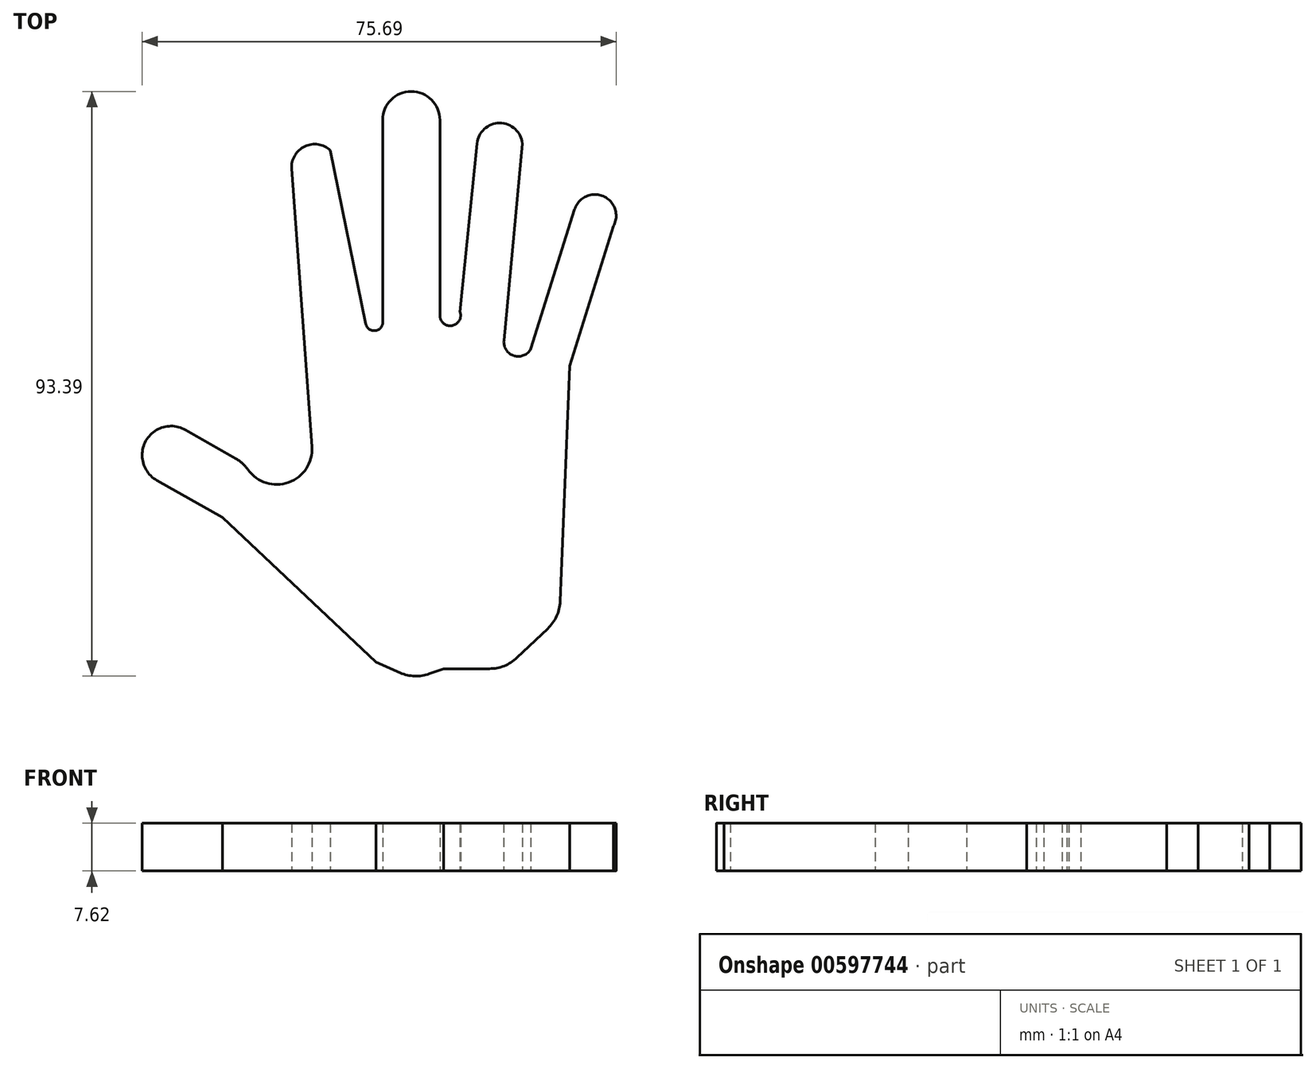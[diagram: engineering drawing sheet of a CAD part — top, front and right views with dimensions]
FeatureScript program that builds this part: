
annotation { "Feature Type Name" : "Feature", "Feature Type Description" : "" }
export const myFeature = defineFeature(function(context is Context, id is Id, definition is map)
    precondition{}
    {
        {
            var Q0;
            Q0=qCreatedBy(makeId("Top.planeOp"),FACE);
            var sketch = newSketch(context, id + "F0", { "sketchPlane" : qUnion([Q0])});
            skLineSegment(sketch, "E0", {"start": v(-29.58, 47.06) * mm, "end": v(-26.36, 2.69) * mm});
            skLineSegment(sketch, "E1", {"start": v(-23.4, 50.02) * mm, "end": v(-17.75, 22.32) * mm});
            skLineSegment(sketch, "E2", {"start": v(-15.06, 54.86) * mm, "end": v(-15.06, 22.32) * mm});
            skLineSegment(sketch, "E3", {"start": v(-5.92, 54.86) * mm, "end": v(-5.92, 23.67) * mm});
            skLineSegment(sketch, "E4", {"start": v(0, 51.1) * mm, "end": v(-2.69, 24.2) * mm});
            skLineSegment(sketch, "E5", {"start": v(7.26, 51.1) * mm, "end": v(4.3, 19.63) * mm});
            skLineSegment(sketch, "E6", {"start": v(15.6, 40.61) * mm, "end": v(8.61, 18.31) * mm});
            skLineSegment(sketch, "E7", {"start": v(21.78, 37.92) * mm, "end": v(14.8, 15.6) * mm});
            skLineSegment(sketch, "E8", {"start": v(14.8, 15.6) * mm, "end": v(13.27, -22) * mm});
            skLineSegment(sketch, "E9", {"start": v(-40.61, -8.6) * mm, "end": v(-16.14, -31.74) * mm});
            skLineSegment(sketch, "E10", {"start": v(-40.61, -8.6) * mm, "end": v(-51.1, -2.69) * mm});
            skLineSegment(sketch, "E11", {"start": v(11.3, -26.36) * mm, "end": v(6.37, -31.02) * mm});
            skLineSegment(sketch, "E12", {"start": v(2, -32.76) * mm, "end": v(-5.34, -32.76) * mm});
            skLineSegment(sketch, "E13", {"start": v(-5.34, -32.76) * mm, "end": v(-7.58, -33.57) * mm});
            skLineSegment(sketch, "E14", {"start": v(-12.26, -33.42) * mm, "end": v(-16.14, -31.74) * mm});
            skPoint(sketch, "E15.visualSharp", {"position": v(-9.95, -34.42) * mm});
            skArc(sketch, "E15.filletArc", {"start": v(-12.26, -33.42) * mm, "mid": v(-9.94, -33.94) * mm, "end": v(-7.58, -33.57) * mm});
            skPoint(sketch, "E16.visualSharp", {"position": v(4.53, -32.76) * mm});
            skArc(sketch, "E16.filletArc", {"start": v(2, -32.76) * mm, "mid": v(4.35, -32.31) * mm, "end": v(6.37, -31.02) * mm});
            skPoint(sketch, "E17.visualSharp", {"position": v(13.17, -24.58) * mm});
            skArc(sketch, "E17.filletArc", {"start": v(11.3, -26.36) * mm, "mid": v(12.7, -24.37) * mm, "end": v(13.27, -22) * mm});
            skArc(sketch, "E18", {"start": v(-17.75, 22.32) * mm, "mid": v(-16.4, 21.22) * mm, "end": v(-15.06, 22.32) * mm});
            skArc(sketch, "E19", {"start": v(-5.92, 23.67) * mm, "mid": v(-3.99, 22.03) * mm, "end": v(-2.69, 24.2) * mm});
            skArc(sketch, "E20", {"start": v(4.3, 19.63) * mm, "mid": v(5.92, 17.22) * mm, "end": v(8.61, 18.31) * mm});
            skArc(sketch, "E21", {"start": v(-26.36, 2.69) * mm, "mid": v(-30.06, -3.01) * mm, "end": v(-36.55, -1) * mm});
            skArc(sketch, "E22", {"start": v(-51.1, -2.69) * mm, "mid": v(-52.85, 3.64) * mm, "end": v(-46.53, 5.38) * mm});
            skLineSegment(sketch, "E23", {"start": v(-46.53, 5.38) * mm, "end": v(-38.56, 0.83) * mm});
            skPoint(sketch, "E24.visualSharp", {"position": v(-37.11, 0) * mm});
            skArc(sketch, "E24.filletArc", {"start": v(-36.55, -1) * mm, "mid": v(-37.46, 0.03) * mm, "end": v(-38.56, 0.83) * mm});
            skArc(sketch, "E25", {"start": v(-29.58, 47.06) * mm, "mid": v(-27.5, 50.65) * mm, "end": v(-23.4, 50.02) * mm});
            skArc(sketch, "E26", {"start": v(-15.06, 54.86) * mm, "mid": v(-10.49, 59.44) * mm, "end": v(-5.92, 54.86) * mm});
            skArc(sketch, "E27", {"start": v(0, 51.1) * mm, "mid": v(3.63, 54.38) * mm, "end": v(7.26, 51.1) * mm});
            skArc(sketch, "E28", {"start": v(15.6, 40.61) * mm, "mid": v(20.19, 42.7) * mm, "end": v(21.78, 37.92) * mm});
            skSolve(sketch);
        }
        {
            var Q0;
            Q0=makeQuery(id+"F0.imprint","IMPRINT",FACE,{"disambiguationData":[TD([[makeQuery(id+"F0.imprint","IMPRINT",EDGE,{"derivedFrom":sQuery(id+"F0.wireOp",EDGE,"E0")}),1.0]])]});
            var sketch = newSketch(context, id + "F1", { "sketchPlane" : qUnion([Q0])});
            skSolve(sketch);
        }
        {
            var Q0;
            Q0=makeQuery(id+"F0.imprint","IMPRINT",FACE,{"disambiguationData":[TD([[makeQuery(id+"F0.imprint","IMPRINT",EDGE,{"derivedFrom":sQuery(id+"F0.wireOp",EDGE,"E0")}),1.0]])]});
            var Q1;
            Q1=makeQuery(id+"F1.imprint","IMPRINT",FACE,{"disambiguationData":[TD([[makeQuery(id+"F1.imprint","IMPRINT",EDGE,{"derivedFrom":makeQuery(id+"F0.imprint","IMPRINT",EDGE,{"derivedFrom":sQuery(id+"F0.wireOp",EDGE,"E0")})}),1.0]])]});
            extrude(context, id + "F2", {"entities" : qUnion([Q0, Q1]), "depth" : 7.62 * mm, "offsetDistance" : 25.4 * mm});
        }
    });
